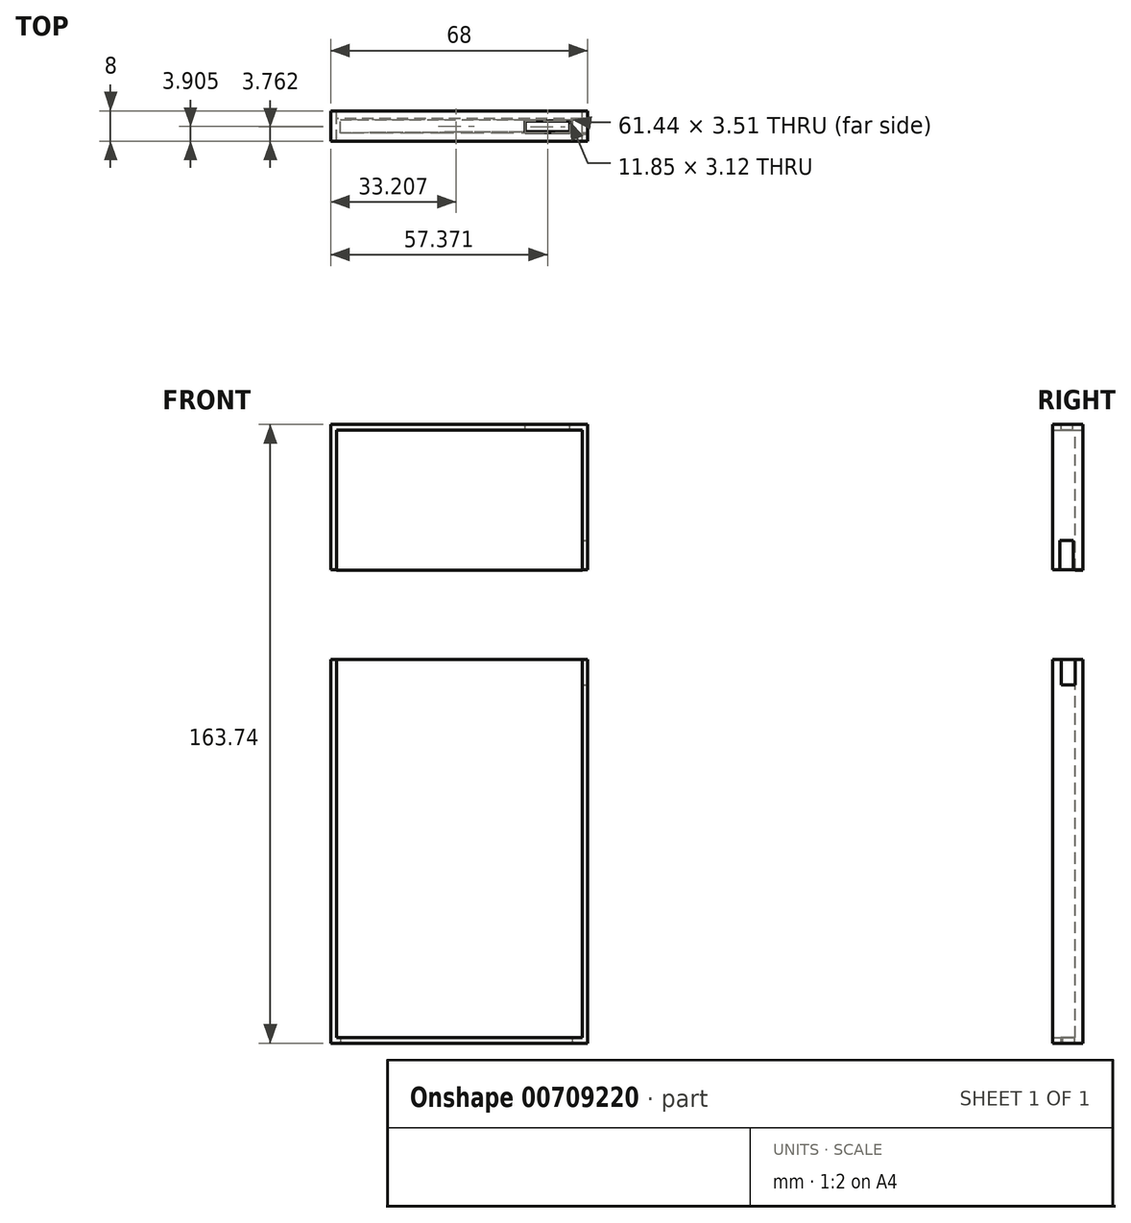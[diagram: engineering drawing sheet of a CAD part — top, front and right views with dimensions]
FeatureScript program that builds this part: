
annotation { "Feature Type Name" : "Feature", "Feature Type Description" : "" }
export const myFeature = defineFeature(function(context is Context, id is Id, definition is map)
    precondition{}
    {
        {
            var Q0;
            Q0=qCreatedBy(makeId("Front.planeOp"),FACE);
            var sketch = newSketch(context, id + "F0", { "sketchPlane" : qUnion([Q0])});
            skLineSegment(sketch, "E0.bottom", {"start": v(32.5, 50) * mm, "end": v(-32.5, 50) * mm});
            skLineSegment(sketch, "E0.top", {"start": v(32.5, -50) * mm, "end": v(-32.5, -50) * mm});
            skLineSegment(sketch, "E0.left", {"start": v(32.5, 50) * mm, "end": v(32.5, -50) * mm});
            skLineSegment(sketch, "E0.right", {"start": v(-32.5, 50) * mm, "end": v(-32.5, -50) * mm});
            skPoint(sketch, "E0.middle", {"position": v(0, 0) * mm});
            skLineSegment(sketch, "E1.bottom", {"start": v(32.5, 73.74) * mm, "end": v(-32.5, 73.74) * mm});
            skLineSegment(sketch, "E1.top", {"start": v(32.5, 110.74) * mm, "end": v(-32.5, 110.74) * mm});
            skLineSegment(sketch, "E1.left", {"start": v(32.5, 73.74) * mm, "end": v(32.5, 110.74) * mm});
            skLineSegment(sketch, "E1.right", {"start": v(-32.5, 73.74) * mm, "end": v(-32.5, 110.74) * mm});
            skPoint(sketch, "E1.middle", {"position": v(0, 92.24) * mm});
            skLineSegment(sketch, "E2", {"start": v(32.5, 50) * mm, "end": v(34, 50) * mm});
            skLineSegment(sketch, "E3", {"start": v(34, 50) * mm, "end": v(34, -51.5) * mm});
            skLineSegment(sketch, "E4", {"start": v(34, -51.5) * mm, "end": v(-34, -51.5) * mm});
            skLineSegment(sketch, "E5", {"start": v(-34, -51.5) * mm, "end": v(-34, 50) * mm});
            skLineSegment(sketch, "E6", {"start": v(-34, 50) * mm, "end": v(-32.5, 50) * mm});
            skLineSegment(sketch, "E7", {"start": v(32.5, 73.74) * mm, "end": v(34, 73.74) * mm});
            skLineSegment(sketch, "E8", {"start": v(34, 73.74) * mm, "end": v(34, 112.24) * mm});
            skLineSegment(sketch, "E9", {"start": v(34, 112.24) * mm, "end": v(-34, 112.24) * mm});
            skLineSegment(sketch, "E10", {"start": v(-34, 112.24) * mm, "end": v(-34, 73.74) * mm});
            skLineSegment(sketch, "E11", {"start": v(-34, 73.74) * mm, "end": v(-32.5, 73.74) * mm});
            skSolve(sketch);
        }
        {
            var Q0;
            Q0=makeQuery(id+"F0.imprint","IMPRINT",FACE,{"disambiguationData":[TD([[makeQuery(id+"F0.imprint","IMPRINT",EDGE,{"derivedFrom":sQuery(id+"F0.wireOp",EDGE,"E1.top")}),-1.0]])]});
            var Q1;
            Q1=makeQuery(id+"F0.imprint","IMPRINT",FACE,{"disambiguationData":[TD([[makeQuery(id+"F0.imprint","IMPRINT",EDGE,{"derivedFrom":sQuery(id+"F0.wireOp",EDGE,"E0.top")}),1.0]])]});
            extrude(context, id + "F1", {"entities" : qUnion([Q0, Q1]), "depth" : 8 * mm, "offsetDistance" : 25 * mm});
        }
        {
            var Q0;
            Q0=qCreatedBy(makeId("Front.planeOp"),FACE);
            var sketch = newSketch(context, id + "F2", { "sketchPlane" : qUnion([Q0])});
            skLineSegment(sketch, "E12.bottom", {"start": v(32.5, -50) * mm, "end": v(-32.5, -50) * mm});
            skLineSegment(sketch, "E12.top", {"start": v(32.5, 50) * mm, "end": v(-32.5, 50) * mm});
            skLineSegment(sketch, "E12.left", {"start": v(32.5, -50) * mm, "end": v(32.5, 50) * mm});
            skLineSegment(sketch, "E12.right", {"start": v(-32.5, -50) * mm, "end": v(-32.5, 50) * mm});
            skPoint(sketch, "E12.middle", {"position": v(0, 0) * mm});
            skSolve(sketch);
        }
        {
            var Q0;
            Q0=makeQuery(id+"F2.imprint","IMPRINT",FACE,{"disambiguationData":[TD([[makeQuery(id+"F2.imprint","IMPRINT",EDGE,{"derivedFrom":sQuery(id+"F2.wireOp",EDGE,"E12.bottom")}),-1.0]])]});
            extrude(context, id + "F3", {"entities" : qUnion([Q0]), "operationType" : NewBodyOperationType.ADD, "depth" : 2 * mm, "offsetDistance" : 25 * mm});
        }
        {
            var Q0;
            Q0=qCreatedBy(makeId("Front.planeOp"),FACE);
            var sketch = newSketch(context, id + "F4", { "sketchPlane" : qUnion([Q0])});
            skLineSegment(sketch, "E13.bottom", {"start": v(32.5, 73.7) * mm, "end": v(-32.5, 73.7) * mm});
            skLineSegment(sketch, "E13.top", {"start": v(32.5, 110.7) * mm, "end": v(-32.5, 110.7) * mm});
            skLineSegment(sketch, "E13.left", {"start": v(32.5, 73.7) * mm, "end": v(32.5, 110.7) * mm});
            skLineSegment(sketch, "E13.right", {"start": v(-32.5, 73.7) * mm, "end": v(-32.5, 110.7) * mm});
            skPoint(sketch, "E13.middle", {"position": v(0, 92.2) * mm});
            skSolve(sketch);
        }
        {
            var Q0;
            Q0=makeQuery(id+"F4.imprint","IMPRINT",FACE,{"disambiguationData":[TD([[makeQuery(id+"F4.imprint","IMPRINT",EDGE,{"derivedFrom":sQuery(id+"F4.wireOp",EDGE,"E13.bottom")}),-1.0]])]});
            extrude(context, id + "F5", {"entities" : qUnion([Q0]), "operationType" : NewBodyOperationType.ADD, "depth" : 2 * mm, "offsetDistance" : 25 * mm});
        }
        {
            var Q0;
            Q0=makeQuery(id+"F1.opExtrude","SWEPT_FACE",FACE,{"disambiguationData":[OSD([sQuery(id+"F0.wireOp",EDGE,"E4")])]});
            var sketch = newSketch(context, id + "F6", { "sketchPlane" : qUnion([Q0])});
            skLineSegment(sketch, "E14", {"start": v(-31.51, 5.85) * mm, "end": v(-31.51, 2.34) * mm});
            skLineSegment(sketch, "E15", {"start": v(-31.51, 2.34) * mm, "end": v(29.93, 2.34) * mm});
            skLineSegment(sketch, "E16", {"start": v(29.93, 2.34) * mm, "end": v(29.93, 5.48) * mm});
            skLineSegment(sketch, "E17", {"start": v(29.93, 5.48) * mm, "end": v(-31.51, 5.85) * mm});
            skSolve(sketch);
        }
        {
            var Q0;
            Q0=makeQuery(id+"F6.imprint","IMPRINT",FACE,{"disambiguationData":[TD([[makeQuery(id+"F6.imprint","IMPRINT",EDGE,{"derivedFrom":sQuery(id+"F6.wireOp",EDGE,"E14")}),1.0]])]});
            extrude(context, id + "F7", {"entities" : qUnion([Q0]), "operationType" : NewBodyOperationType.REMOVE, "oppositeDirection" : true, "depth" : 1.5 * mm, "offsetDistance" : 25 * mm});
        }
        {
            var Q0;
            Q0=makeQuery(id+"F1.opExtrude","SWEPT_FACE",FACE,{"disambiguationData":[OSD([sQuery(id+"F0.wireOp",EDGE,"E9")])]});
            var sketch = newSketch(context, id + "F8", { "sketchPlane" : qUnion([Q0])});
            skLineSegment(sketch, "E18", {"start": v(17.45, -2.68) * mm, "end": v(17.45, -5.8) * mm});
            skLineSegment(sketch, "E19", {"start": v(17.45, -5.8) * mm, "end": v(29.3, -5.8) * mm});
            skLineSegment(sketch, "E20", {"start": v(29.3, -5.8) * mm, "end": v(29.3, -2.7) * mm});
            skLineSegment(sketch, "E21", {"start": v(29.3, -2.7) * mm, "end": v(17.45, -2.68) * mm});
            skSolve(sketch);
        }
        {
            var Q0;
            Q0=makeQuery(id+"F8.imprint","IMPRINT",FACE,{"disambiguationData":[TD([[makeQuery(id+"F8.imprint","IMPRINT",EDGE,{"derivedFrom":sQuery(id+"F8.wireOp",EDGE,"E18")}),1.0]])]});
            extrude(context, id + "F9", {"entities" : qUnion([Q0]), "operationType" : NewBodyOperationType.REMOVE, "oppositeDirection" : true, "depth" : 1.5 * mm, "offsetDistance" : 25 * mm});
        }
        {
            var Q0;
            Q0=makeQuery(id+"F1.opExtrude","SWEPT_FACE",FACE,{"disambiguationData":[OSD([sQuery(id+"F0.wireOp",EDGE,"E8")])]});
            var sketch = newSketch(context, id + "F10", { "sketchPlane" : qUnion([Q0])});
            skLineSegment(sketch, "E22", {"start": v(-6.08, 73.74) * mm, "end": v(-6.08, 81.52) * mm});
            skLineSegment(sketch, "E23", {"start": v(-6.08, 81.52) * mm, "end": v(-2.54, 81.52) * mm});
            skLineSegment(sketch, "E24", {"start": v(-2.54, 81.52) * mm, "end": v(-2.54, 73.74) * mm});
            skLineSegment(sketch, "E25", {"start": v(-2.54, 73.74) * mm, "end": v(-6.08, 73.74) * mm});
            skSolve(sketch);
        }
        {
            var Q0;
            Q0=makeQuery(id+"F10.imprint","IMPRINT",FACE,{"disambiguationData":[TD([[makeQuery(id+"F10.imprint","IMPRINT",EDGE,{"derivedFrom":sQuery(id+"F10.wireOp",EDGE,"E22")}),-1.0]])]});
            extrude(context, id + "F11", {"entities" : qUnion([Q0]), "operationType" : NewBodyOperationType.REMOVE, "oppositeDirection" : true, "depth" : 1.5 * mm, "offsetDistance" : 25 * mm});
        }
        {
            var Q0;
            Q0=makeQuery(id+"F1.opExtrude","SWEPT_FACE",FACE,{"disambiguationData":[OSD([sQuery(id+"F0.wireOp",EDGE,"E3")])]});
            var sketch = newSketch(context, id + "F12", { "sketchPlane" : qUnion([Q0])});
            skLineSegment(sketch, "E26", {"start": v(-5.75, 50) * mm, "end": v(-5.75, 43.27) * mm});
            skLineSegment(sketch, "E27", {"start": v(-5.75, 43.27) * mm, "end": v(-2.11, 43.27) * mm});
            skLineSegment(sketch, "E28", {"start": v(-2.11, 43.27) * mm, "end": v(-2.11, 50) * mm});
            skLineSegment(sketch, "E29", {"start": v(-2.11, 50) * mm, "end": v(-5.75, 50) * mm});
            skSolve(sketch);
        }
        {
            var Q0;
            Q0=makeQuery(id+"F12.imprint","IMPRINT",FACE,{"disambiguationData":[TD([[makeQuery(id+"F12.imprint","IMPRINT",EDGE,{"derivedFrom":sQuery(id+"F12.wireOp",EDGE,"E26")}),1.0]])]});
            extrude(context, id + "F13", {"entities" : qUnion([Q0]), "operationType" : NewBodyOperationType.REMOVE, "oppositeDirection" : true, "depth" : 1.5 * mm, "offsetDistance" : 25 * mm});
        }
    });
